# Revit family: Mechanism_Kit-Simon-K45-Watertight_Floor
name_source: partatom
category: Electrical Fixtures
revit_build: Autodesk Revit 2014 (Build: 20130308_1515(x64)
units: mm (PartAtom-declared; Revit-internal decimal feet)

## types (1)
- 1xSchuko, 1xRJ45
    Box depth = 69 mm
    Cost = 136.03€
    Current = 16 A
    Default Elevation = 1219 mm
    Description = IP 66 watertight floor box and manual lock with 1 Schuko outlet and 1 RJ45 UTP category 6 connector.
    Element Material = 9003 Signal white
    Frame Material = Stainless Steel, Brushed
    Manufacturer = SIMON
    Manufacturing material = Stainless steel (AISI 304 ferritic stainless steel type)
    Overall dimensions = 135x135 mm
    Protection against impacts = IK08
    Protection against solid and liquid bodies = IP66
    RJ45 compatibility figure = Keystone
    Series = K45
    Technical data sheet = http://www.simon.es
    Type Comments = Adjustment height floor box frrom 70 and 100 mm. Free internal space range: From 13 to 38 mm
    URL = http://www.simon.es
    Voice and data connectors type = RJ45

## geometry (parser evidence)
native form markers: Blend x1, Sweep x1
no freeform markers — native parametric forms only
